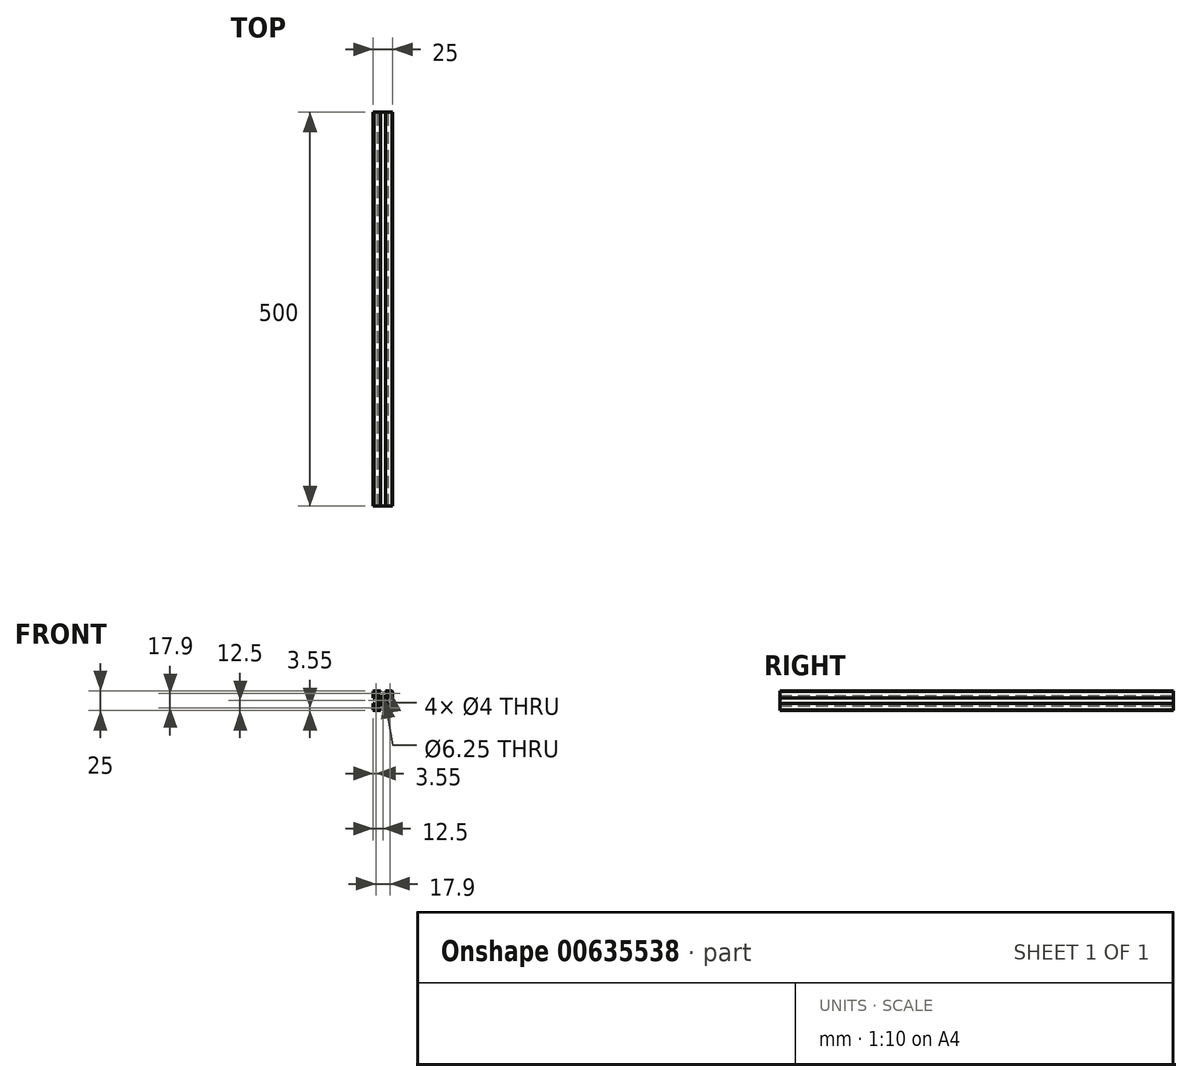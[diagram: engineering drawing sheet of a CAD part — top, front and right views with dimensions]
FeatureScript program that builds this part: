
annotation { "Feature Type Name" : "Feature", "Feature Type Description" : "" }
export const myFeature = defineFeature(function(context is Context, id is Id, definition is map)
    precondition{}
    {
        {
            var Q0;
            Q0=qCreatedBy(makeId("Front.planeOp"),FACE);
            var sketch = newSketch(context, id + "F0", { "sketchPlane" : qUnion([Q0])});
            skLineSegment(sketch, "E0.bottom", {"start": v(0, 0) * mm, "end": v(12.5, 0) * mm, "construction": true});
            skLineSegment(sketch, "E0.top", {"start": v(0, -12.5) * mm, "end": v(12.5, -12.5) * mm, "construction": true});
            skLineSegment(sketch, "E0.left", {"start": v(0, 0) * mm, "end": v(0, -12.5) * mm, "construction": true});
            skLineSegment(sketch, "E0.right", {"start": v(12.5, 0) * mm, "end": v(12.5, -12.5) * mm, "construction": true});
            skLineSegment(sketch, "E1", {"start": v(0, -3.25) * mm, "end": v(12.5, -3.25) * mm, "construction": true});
            skLineSegment(sketch, "E2", {"start": v(0, 0) * mm, "end": v(12.5, -12.5) * mm, "construction": true});
            skLineSegment(sketch, "E3", {"start": v(3.25, 0) * mm, "end": v(3.25, -12.5) * mm, "construction": true});
            skLineSegment(sketch, "E4", {"start": v(12.5, -3.25) * mm, "end": v(12.5, -12.5) * mm});
            skLineSegment(sketch, "E5", {"start": v(3.25, -12.5) * mm, "end": v(12.5, -12.5) * mm});
            skLineSegment(sketch, "E6", {"start": v(0, -5.4) * mm, "end": v(12.5, -5.4) * mm, "construction": true});
            skLineSegment(sketch, "E7", {"start": v(10.8, -3.25) * mm, "end": v(10.8, -12.5) * mm, "construction": true});
            skLineSegment(sketch, "E8", {"start": v(12.5, -3.25) * mm, "end": v(10.8, -3.25) * mm});
            skLineSegment(sketch, "E9", {"start": v(10.8, -3.25) * mm, "end": v(10.8, -5.4) * mm});
            skLineSegment(sketch, "E10", {"start": v(5.4, 0) * mm, "end": v(5.4, -12.5) * mm, "construction": true});
            skLineSegment(sketch, "E11", {"start": v(0, -10.8) * mm, "end": v(12.5, -10.8) * mm, "construction": true});
            skLineSegment(sketch, "E12", {"start": v(3.25, -12.5) * mm, "end": v(3.25, -10.8) * mm});
            skLineSegment(sketch, "E13", {"start": v(3.25, -10.8) * mm, "end": v(5.4, -10.8) * mm});
            skLineSegment(sketch, "E14.MirrorCS", {"start": v(3.25, 10.8) * mm, "end": v(5.4, 10.8) * mm});
            skLineSegment(sketch, "E15.MirrorCS", {"start": v(3.25, 12.5) * mm, "end": v(3.25, 10.8) * mm});
            skLineSegment(sketch, "E16.MirrorCS", {"start": v(10.8, 3.25) * mm, "end": v(10.8, 5.4) * mm});
            skLineSegment(sketch, "E17.MirrorCS", {"start": v(12.5, 3.25) * mm, "end": v(10.8, 3.25) * mm});
            skLineSegment(sketch, "E18.MirrorCS", {"start": v(12.5, 3.25) * mm, "end": v(12.5, 12.5) * mm});
            skLineSegment(sketch, "E19.MirrorCS", {"start": v(3.25, 12.5) * mm, "end": v(12.5, 12.5) * mm});
            skLineSegment(sketch, "E20.MirrorCS", {"start": v(-3.25, 10.8) * mm, "end": v(-5.4, 10.8) * mm});
            skLineSegment(sketch, "E21.MirrorCS", {"start": v(-3.25, 12.5) * mm, "end": v(-3.25, 10.8) * mm});
            skLineSegment(sketch, "E22.MirrorCS", {"start": v(-3.25, 12.5) * mm, "end": v(-12.5, 12.5) * mm});
            skLineSegment(sketch, "E23.MirrorCS", {"start": v(-12.5, 3.25) * mm, "end": v(-12.5, 12.5) * mm});
            skLineSegment(sketch, "E24.MirrorCS", {"start": v(-12.5, 3.25) * mm, "end": v(-10.8, 3.25) * mm});
            skLineSegment(sketch, "E25.MirrorCS", {"start": v(-10.8, 3.25) * mm, "end": v(-10.8, 5.4) * mm});
            skLineSegment(sketch, "E26.MirrorCS", {"start": v(-10.8, -3.25) * mm, "end": v(-10.8, -5.4) * mm});
            skLineSegment(sketch, "E27.MirrorCS", {"start": v(-12.5, -3.25) * mm, "end": v(-10.8, -3.25) * mm});
            skLineSegment(sketch, "E28.MirrorCS", {"start": v(-12.5, -3.25) * mm, "end": v(-12.5, -12.5) * mm});
            skLineSegment(sketch, "E29.MirrorCS", {"start": v(-3.25, -12.5) * mm, "end": v(-12.5, -12.5) * mm});
            skLineSegment(sketch, "E30.MirrorCS", {"start": v(-3.25, -12.5) * mm, "end": v(-3.25, -10.8) * mm});
            skLineSegment(sketch, "E31.MirrorCS", {"start": v(-3.25, -10.8) * mm, "end": v(-5.4, -10.8) * mm});
            skLineSegment(sketch, "E32", {"start": v(6.25, -5.4) * mm, "end": v(6.25, -12.5) * mm, "construction": true});
            skLineSegment(sketch, "E33", {"start": v(0, -6.25) * mm, "end": v(6.25, -6.25) * mm, "construction": true});
            skLineSegment(sketch, "E34", {"start": v(6.25, -5.4) * mm, "end": v(10.8, -5.4) * mm});
            skLineSegment(sketch, "E35", {"start": v(5.4, -10.8) * mm, "end": v(5.4, -6.25) * mm});
            skLineSegment(sketch, "E36.MirrorCS", {"start": v(6.25, 5.4) * mm, "end": v(10.8, 5.4) * mm});
            skLineSegment(sketch, "E37.MirrorCS", {"start": v(5.4, 10.8) * mm, "end": v(5.4, 6.25) * mm});
            skLineSegment(sketch, "E38.MirrorCS", {"start": v(-5.4, 10.8) * mm, "end": v(-5.4, 6.25) * mm});
            skLineSegment(sketch, "E39.MirrorCS", {"start": v(-6.25, 5.4) * mm, "end": v(-10.8, 5.4) * mm});
            skLineSegment(sketch, "E40.MirrorCS", {"start": v(-6.25, -5.4) * mm, "end": v(-10.8, -5.4) * mm});
            skLineSegment(sketch, "E41.MirrorCS", {"start": v(-5.4, -10.8) * mm, "end": v(-5.4, -6.25) * mm});
            skArc(sketch, "E42", {"start": v(5.4, -6.25) * mm, "mid": v(0, -5.4) * mm, "end": v(-5.4, -6.25) * mm});
            skArc(sketch, "E43.MirrorCS", {"start": v(5.4, 6.25) * mm, "mid": v(0, 5.4) * mm, "end": v(-5.4, 6.25) * mm});
            skArc(sketch, "E44", {"start": v(6.25, 5.4) * mm, "mid": v(5.4, 0) * mm, "end": v(6.25, -5.4) * mm});
            skArc(sketch, "E45.MirrorCS", {"start": v(-6.25, 5.4) * mm, "mid": v(-5.4, 0) * mm, "end": v(-6.25, -5.4) * mm});
            skLineSegment(sketch, "E46", {"start": v(12.5, -5.4) * mm, "end": v(8.95, -8.95) * mm, "construction": true});
            skCircle(sketch, "E47", {"center": v(8.95, -8.95) * mm, "radius": 2 * mm, "construction": true});
            skCircle(sketch, "E48.MirrorC", {"center": v(8.95, 8.95) * mm, "radius": 2 * mm, "construction": true});
            skCircle(sketch, "E49.MirrorC", {"center": v(-8.95, 8.95) * mm, "radius": 2 * mm, "construction": true});
            skCircle(sketch, "E50.MirrorC", {"center": v(-8.95, -8.95) * mm, "radius": 2 * mm, "construction": true});
            skCircle(sketch, "E51", {"center": v(0, 0) * mm, "radius": 3.12 * mm, "construction": true});
            skSolve(sketch);
        }
        {
            var Q0;
            Q0=makeQuery(id+"F0.imprint","IMPRINT",FACE,{"disambiguationData":[TD([[makeQuery(id+"F0.imprint","IMPRINT",EDGE,{"derivedFrom":sQuery(id+"F0.wireOp",EDGE,"E4")}),-1.0]])]});
            extrude(context, id + "F1", {"entities" : qUnion([Q0]), "depth" : 500 * mm, "offsetDistance" : 25 * mm});
        }
        {
            var Q0;
            Q0=makeQuery(id+"F1.opExtrude","SWEPT_EDGE",EDGE,{"disambiguationData":[OSD([sQuery(id+"F0.wireOp",EDGE,"E22.MirrorCS"),sQuery(id+"F0.wireOp",EDGE,"E23.MirrorCS")])]});
            chamfer(context, id + "F2", {"entities" : qUnion([Q0]), "width" : 1 * mm, "tangentPropagation" : true});
        }
        {
            var Q0;
            Q0=makeQuery(id+"F1.opExtrude","SWEPT_EDGE",EDGE,{"disambiguationData":[OSD([sQuery(id+"F0.wireOp",EDGE,"E18.MirrorCS"),sQuery(id+"F0.wireOp",EDGE,"E19.MirrorCS")])]});
            var Q1;
            Q1=makeQuery(id+"F1.opExtrude","SWEPT_EDGE",EDGE,{"disambiguationData":[OSD([sQuery(id+"F0.wireOp",EDGE,"E4"),sQuery(id+"F0.wireOp",EDGE,"E5")])]});
            var Q2;
            Q2=makeQuery(id+"F1.opExtrude","SWEPT_EDGE",EDGE,{"disambiguationData":[OSD([sQuery(id+"F0.wireOp",EDGE,"E28.MirrorCS"),sQuery(id+"F0.wireOp",EDGE,"E29.MirrorCS")])]});
            chamfer(context, id + "F3", {"entities" : qUnion([Q0, Q1, Q2]), "width" : 1 * mm, "tangentPropagation" : true});
        }
        {
            var Q0;
            Q0=makeQuery(id+"F1.opExtrude","SWEPT_EDGE",EDGE,{"disambiguationData":[OSD([sQuery(id+"F0.wireOp",EDGE,"E14.MirrorCS"),sQuery(id+"F0.wireOp",EDGE,"E15.MirrorCS")])]});
            var Q1;
            Q1=makeQuery(id+"F1.opExtrude","SWEPT_EDGE",EDGE,{"disambiguationData":[OSD([sQuery(id+"F0.wireOp",EDGE,"E16.MirrorCS"),sQuery(id+"F0.wireOp",EDGE,"E17.MirrorCS")])]});
            var Q2;
            Q2=makeQuery(id+"F1.opExtrude","SWEPT_EDGE",EDGE,{"disambiguationData":[OSD([sQuery(id+"F0.wireOp",EDGE,"E8"),sQuery(id+"F0.wireOp",EDGE,"E9")])]});
            var Q3;
            Q3=makeQuery(id+"F1.opExtrude","SWEPT_EDGE",EDGE,{"disambiguationData":[OSD([sQuery(id+"F0.wireOp",EDGE,"E12"),sQuery(id+"F0.wireOp",EDGE,"E13")])]});
            var Q4;
            Q4=makeQuery(id+"F1.opExtrude","SWEPT_EDGE",EDGE,{"disambiguationData":[OSD([sQuery(id+"F0.wireOp",EDGE,"E30.MirrorCS"),sQuery(id+"F0.wireOp",EDGE,"E31.MirrorCS")])]});
            var Q5;
            Q5=makeQuery(id+"F1.opExtrude","SWEPT_EDGE",EDGE,{"disambiguationData":[OSD([sQuery(id+"F0.wireOp",EDGE,"E26.MirrorCS"),sQuery(id+"F0.wireOp",EDGE,"E27.MirrorCS")])]});
            var Q6;
            Q6=makeQuery(id+"F1.opExtrude","SWEPT_EDGE",EDGE,{"disambiguationData":[OSD([sQuery(id+"F0.wireOp",EDGE,"E20.MirrorCS"),sQuery(id+"F0.wireOp",EDGE,"E21.MirrorCS")])]});
            var Q7;
            Q7=makeQuery(id+"F1.opExtrude","SWEPT_EDGE",EDGE,{"disambiguationData":[OSD([sQuery(id+"F0.wireOp",EDGE,"E24.MirrorCS"),sQuery(id+"F0.wireOp",EDGE,"E25.MirrorCS")])]});
            chamfer(context, id + "F4", {"entities" : qUnion([Q0, Q1, Q2, Q3, Q4, Q5, Q6, Q7]), "width" : 1 * mm, "tangentPropagation" : true});
        }
        {
            var Q0;
            Q0=sQuery(id+"F0.wireOp",VERTEX,"E47.center");
            var Q1;
            Q1=makeQuery(id+"F1.opExtrude","SWEPT_BODY",BODY,{"disambiguationData":[OSD([sQuery(id+"F0.wireOp",EDGE,"E4"),sQuery(id+"F0.wireOp",EDGE,"E5"),sQuery(id+"F0.wireOp",EDGE,"E8"),sQuery(id+"F0.wireOp",EDGE,"E9"),sQuery(id+"F0.wireOp",EDGE,"E12"),sQuery(id+"F0.wireOp",EDGE,"E13"),sQuery(id+"F0.wireOp",EDGE,"E14.MirrorCS"),sQuery(id+"F0.wireOp",EDGE,"E15.MirrorCS"),sQuery(id+"F0.wireOp",EDGE,"E16.MirrorCS"),sQuery(id+"F0.wireOp",EDGE,"E17.MirrorCS"),sQuery(id+"F0.wireOp",EDGE,"E18.MirrorCS"),sQuery(id+"F0.wireOp",EDGE,"E19.MirrorCS"),sQuery(id+"F0.wireOp",EDGE,"E20.MirrorCS"),sQuery(id+"F0.wireOp",EDGE,"E21.MirrorCS"),sQuery(id+"F0.wireOp",EDGE,"E22.MirrorCS"),sQuery(id+"F0.wireOp",EDGE,"E23.MirrorCS"),sQuery(id+"F0.wireOp",EDGE,"E24.MirrorCS"),sQuery(id+"F0.wireOp",EDGE,"E25.MirrorCS"),sQuery(id+"F0.wireOp",EDGE,"E26.MirrorCS"),sQuery(id+"F0.wireOp",EDGE,"E27.MirrorCS"),sQuery(id+"F0.wireOp",EDGE,"E28.MirrorCS"),sQuery(id+"F0.wireOp",EDGE,"E29.MirrorCS"),sQuery(id+"F0.wireOp",EDGE,"E30.MirrorCS"),sQuery(id+"F0.wireOp",EDGE,"E31.MirrorCS"),sQuery(id+"F0.wireOp",EDGE,"E34"),sQuery(id+"F0.wireOp",EDGE,"E35"),sQuery(id+"F0.wireOp",EDGE,"E36.MirrorCS"),sQuery(id+"F0.wireOp",EDGE,"E37.MirrorCS"),sQuery(id+"F0.wireOp",EDGE,"E38.MirrorCS"),sQuery(id+"F0.wireOp",EDGE,"E39.MirrorCS"),sQuery(id+"F0.wireOp",EDGE,"E40.MirrorCS"),sQuery(id+"F0.wireOp",EDGE,"E41.MirrorCS"),sQuery(id+"F0.wireOp",EDGE,"E42"),sQuery(id+"F0.wireOp",EDGE,"E43.MirrorCS"),sQuery(id+"F0.wireOp",EDGE,"E44"),sQuery(id+"F0.wireOp",EDGE,"E45.MirrorCS")])]});
            hole(context, id + "F5", {"style" : HoleStyle.SIMPLE, "endStyle" : HoleEndStyle.THROUGH, "oppositeDirection" : true, "holeDiameter" : 4 * mm, "majorDiameter" : 5 * mm, "isTappedThrough" : true, "tappedDepth" : 12 * mm, "tapClearance" : 3, "locations" : qUnion([Q0]), "scope" : qUnion([Q1])});
        }
        {
            var Q0;
            Q0=sQuery(id+"F0.wireOp",VERTEX,"E48.MirrorC.center");
            var Q1;
            Q1=makeQuery(id+"F1.opExtrude","SWEPT_BODY",BODY,{"disambiguationData":[OSD([sQuery(id+"F0.wireOp",EDGE,"E4"),sQuery(id+"F0.wireOp",EDGE,"E5"),sQuery(id+"F0.wireOp",EDGE,"E8"),sQuery(id+"F0.wireOp",EDGE,"E9"),sQuery(id+"F0.wireOp",EDGE,"E12"),sQuery(id+"F0.wireOp",EDGE,"E13"),sQuery(id+"F0.wireOp",EDGE,"E14.MirrorCS"),sQuery(id+"F0.wireOp",EDGE,"E15.MirrorCS"),sQuery(id+"F0.wireOp",EDGE,"E16.MirrorCS"),sQuery(id+"F0.wireOp",EDGE,"E17.MirrorCS"),sQuery(id+"F0.wireOp",EDGE,"E18.MirrorCS"),sQuery(id+"F0.wireOp",EDGE,"E19.MirrorCS"),sQuery(id+"F0.wireOp",EDGE,"E20.MirrorCS"),sQuery(id+"F0.wireOp",EDGE,"E21.MirrorCS"),sQuery(id+"F0.wireOp",EDGE,"E22.MirrorCS"),sQuery(id+"F0.wireOp",EDGE,"E23.MirrorCS"),sQuery(id+"F0.wireOp",EDGE,"E24.MirrorCS"),sQuery(id+"F0.wireOp",EDGE,"E25.MirrorCS"),sQuery(id+"F0.wireOp",EDGE,"E26.MirrorCS"),sQuery(id+"F0.wireOp",EDGE,"E27.MirrorCS"),sQuery(id+"F0.wireOp",EDGE,"E28.MirrorCS"),sQuery(id+"F0.wireOp",EDGE,"E29.MirrorCS"),sQuery(id+"F0.wireOp",EDGE,"E30.MirrorCS"),sQuery(id+"F0.wireOp",EDGE,"E31.MirrorCS"),sQuery(id+"F0.wireOp",EDGE,"E34"),sQuery(id+"F0.wireOp",EDGE,"E35"),sQuery(id+"F0.wireOp",EDGE,"E36.MirrorCS"),sQuery(id+"F0.wireOp",EDGE,"E37.MirrorCS"),sQuery(id+"F0.wireOp",EDGE,"E38.MirrorCS"),sQuery(id+"F0.wireOp",EDGE,"E39.MirrorCS"),sQuery(id+"F0.wireOp",EDGE,"E40.MirrorCS"),sQuery(id+"F0.wireOp",EDGE,"E41.MirrorCS"),sQuery(id+"F0.wireOp",EDGE,"E42"),sQuery(id+"F0.wireOp",EDGE,"E43.MirrorCS"),sQuery(id+"F0.wireOp",EDGE,"E44"),sQuery(id+"F0.wireOp",EDGE,"E45.MirrorCS")])]});
            hole(context, id + "F6", {"style" : HoleStyle.SIMPLE, "endStyle" : HoleEndStyle.THROUGH, "oppositeDirection" : true, "holeDiameter" : 4 * mm, "majorDiameter" : 5 * mm, "isTappedThrough" : true, "tappedDepth" : 12 * mm, "tapClearance" : 3, "locations" : qUnion([Q0]), "scope" : qUnion([Q1])});
        }
        {
            var Q0;
            Q0=sQuery(id+"F0.wireOp",VERTEX,"E50.MirrorC.center");
            var Q1;
            Q1=makeQuery(id+"F1.opExtrude","SWEPT_BODY",BODY,{"disambiguationData":[OSD([sQuery(id+"F0.wireOp",EDGE,"E4"),sQuery(id+"F0.wireOp",EDGE,"E5"),sQuery(id+"F0.wireOp",EDGE,"E8"),sQuery(id+"F0.wireOp",EDGE,"E9"),sQuery(id+"F0.wireOp",EDGE,"E12"),sQuery(id+"F0.wireOp",EDGE,"E13"),sQuery(id+"F0.wireOp",EDGE,"E14.MirrorCS"),sQuery(id+"F0.wireOp",EDGE,"E15.MirrorCS"),sQuery(id+"F0.wireOp",EDGE,"E16.MirrorCS"),sQuery(id+"F0.wireOp",EDGE,"E17.MirrorCS"),sQuery(id+"F0.wireOp",EDGE,"E18.MirrorCS"),sQuery(id+"F0.wireOp",EDGE,"E19.MirrorCS"),sQuery(id+"F0.wireOp",EDGE,"E20.MirrorCS"),sQuery(id+"F0.wireOp",EDGE,"E21.MirrorCS"),sQuery(id+"F0.wireOp",EDGE,"E22.MirrorCS"),sQuery(id+"F0.wireOp",EDGE,"E23.MirrorCS"),sQuery(id+"F0.wireOp",EDGE,"E24.MirrorCS"),sQuery(id+"F0.wireOp",EDGE,"E25.MirrorCS"),sQuery(id+"F0.wireOp",EDGE,"E26.MirrorCS"),sQuery(id+"F0.wireOp",EDGE,"E27.MirrorCS"),sQuery(id+"F0.wireOp",EDGE,"E28.MirrorCS"),sQuery(id+"F0.wireOp",EDGE,"E29.MirrorCS"),sQuery(id+"F0.wireOp",EDGE,"E30.MirrorCS"),sQuery(id+"F0.wireOp",EDGE,"E31.MirrorCS"),sQuery(id+"F0.wireOp",EDGE,"E34"),sQuery(id+"F0.wireOp",EDGE,"E35"),sQuery(id+"F0.wireOp",EDGE,"E36.MirrorCS"),sQuery(id+"F0.wireOp",EDGE,"E37.MirrorCS"),sQuery(id+"F0.wireOp",EDGE,"E38.MirrorCS"),sQuery(id+"F0.wireOp",EDGE,"E39.MirrorCS"),sQuery(id+"F0.wireOp",EDGE,"E40.MirrorCS"),sQuery(id+"F0.wireOp",EDGE,"E41.MirrorCS"),sQuery(id+"F0.wireOp",EDGE,"E42"),sQuery(id+"F0.wireOp",EDGE,"E43.MirrorCS"),sQuery(id+"F0.wireOp",EDGE,"E44"),sQuery(id+"F0.wireOp",EDGE,"E45.MirrorCS")])]});
            hole(context, id + "F7", {"style" : HoleStyle.SIMPLE, "endStyle" : HoleEndStyle.THROUGH, "oppositeDirection" : true, "holeDiameter" : 4 * mm, "majorDiameter" : 5 * mm, "isTappedThrough" : true, "tappedDepth" : 12 * mm, "tapClearance" : 3, "locations" : qUnion([Q0]), "scope" : qUnion([Q1])});
        }
        {
            var Q0;
            Q0=sQuery(id+"F0.wireOp",VERTEX,"E49.MirrorC.center");
            var Q1;
            Q1=makeQuery(id+"F1.opExtrude","SWEPT_BODY",BODY,{"disambiguationData":[OSD([sQuery(id+"F0.wireOp",EDGE,"E4"),sQuery(id+"F0.wireOp",EDGE,"E5"),sQuery(id+"F0.wireOp",EDGE,"E8"),sQuery(id+"F0.wireOp",EDGE,"E9"),sQuery(id+"F0.wireOp",EDGE,"E12"),sQuery(id+"F0.wireOp",EDGE,"E13"),sQuery(id+"F0.wireOp",EDGE,"E14.MirrorCS"),sQuery(id+"F0.wireOp",EDGE,"E15.MirrorCS"),sQuery(id+"F0.wireOp",EDGE,"E16.MirrorCS"),sQuery(id+"F0.wireOp",EDGE,"E17.MirrorCS"),sQuery(id+"F0.wireOp",EDGE,"E18.MirrorCS"),sQuery(id+"F0.wireOp",EDGE,"E19.MirrorCS"),sQuery(id+"F0.wireOp",EDGE,"E20.MirrorCS"),sQuery(id+"F0.wireOp",EDGE,"E21.MirrorCS"),sQuery(id+"F0.wireOp",EDGE,"E22.MirrorCS"),sQuery(id+"F0.wireOp",EDGE,"E23.MirrorCS"),sQuery(id+"F0.wireOp",EDGE,"E24.MirrorCS"),sQuery(id+"F0.wireOp",EDGE,"E25.MirrorCS"),sQuery(id+"F0.wireOp",EDGE,"E26.MirrorCS"),sQuery(id+"F0.wireOp",EDGE,"E27.MirrorCS"),sQuery(id+"F0.wireOp",EDGE,"E28.MirrorCS"),sQuery(id+"F0.wireOp",EDGE,"E29.MirrorCS"),sQuery(id+"F0.wireOp",EDGE,"E30.MirrorCS"),sQuery(id+"F0.wireOp",EDGE,"E31.MirrorCS"),sQuery(id+"F0.wireOp",EDGE,"E34"),sQuery(id+"F0.wireOp",EDGE,"E35"),sQuery(id+"F0.wireOp",EDGE,"E36.MirrorCS"),sQuery(id+"F0.wireOp",EDGE,"E37.MirrorCS"),sQuery(id+"F0.wireOp",EDGE,"E38.MirrorCS"),sQuery(id+"F0.wireOp",EDGE,"E39.MirrorCS"),sQuery(id+"F0.wireOp",EDGE,"E40.MirrorCS"),sQuery(id+"F0.wireOp",EDGE,"E41.MirrorCS"),sQuery(id+"F0.wireOp",EDGE,"E42"),sQuery(id+"F0.wireOp",EDGE,"E43.MirrorCS"),sQuery(id+"F0.wireOp",EDGE,"E44"),sQuery(id+"F0.wireOp",EDGE,"E45.MirrorCS")])]});
            hole(context, id + "F8", {"style" : HoleStyle.SIMPLE, "endStyle" : HoleEndStyle.THROUGH, "oppositeDirection" : true, "holeDiameter" : 4 * mm, "majorDiameter" : 5 * mm, "isTappedThrough" : true, "tappedDepth" : 12 * mm, "tapClearance" : 3, "locations" : qUnion([Q0]), "scope" : qUnion([Q1])});
        }
        {
            var Q0;
            Q0=sQuery(id+"F0.wireOp",VERTEX,"E2.start");
            var Q1;
            Q1=makeQuery(id+"F1.opExtrude","SWEPT_BODY",BODY,{"disambiguationData":[OSD([sQuery(id+"F0.wireOp",EDGE,"E4"),sQuery(id+"F0.wireOp",EDGE,"E5"),sQuery(id+"F0.wireOp",EDGE,"E8"),sQuery(id+"F0.wireOp",EDGE,"E9"),sQuery(id+"F0.wireOp",EDGE,"E12"),sQuery(id+"F0.wireOp",EDGE,"E13"),sQuery(id+"F0.wireOp",EDGE,"E14.MirrorCS"),sQuery(id+"F0.wireOp",EDGE,"E15.MirrorCS"),sQuery(id+"F0.wireOp",EDGE,"E16.MirrorCS"),sQuery(id+"F0.wireOp",EDGE,"E17.MirrorCS"),sQuery(id+"F0.wireOp",EDGE,"E18.MirrorCS"),sQuery(id+"F0.wireOp",EDGE,"E19.MirrorCS"),sQuery(id+"F0.wireOp",EDGE,"E20.MirrorCS"),sQuery(id+"F0.wireOp",EDGE,"E21.MirrorCS"),sQuery(id+"F0.wireOp",EDGE,"E22.MirrorCS"),sQuery(id+"F0.wireOp",EDGE,"E23.MirrorCS"),sQuery(id+"F0.wireOp",EDGE,"E24.MirrorCS"),sQuery(id+"F0.wireOp",EDGE,"E25.MirrorCS"),sQuery(id+"F0.wireOp",EDGE,"E26.MirrorCS"),sQuery(id+"F0.wireOp",EDGE,"E27.MirrorCS"),sQuery(id+"F0.wireOp",EDGE,"E28.MirrorCS"),sQuery(id+"F0.wireOp",EDGE,"E29.MirrorCS"),sQuery(id+"F0.wireOp",EDGE,"E30.MirrorCS"),sQuery(id+"F0.wireOp",EDGE,"E31.MirrorCS"),sQuery(id+"F0.wireOp",EDGE,"E34"),sQuery(id+"F0.wireOp",EDGE,"E35"),sQuery(id+"F0.wireOp",EDGE,"E36.MirrorCS"),sQuery(id+"F0.wireOp",EDGE,"E37.MirrorCS"),sQuery(id+"F0.wireOp",EDGE,"E38.MirrorCS"),sQuery(id+"F0.wireOp",EDGE,"E39.MirrorCS"),sQuery(id+"F0.wireOp",EDGE,"E40.MirrorCS"),sQuery(id+"F0.wireOp",EDGE,"E41.MirrorCS"),sQuery(id+"F0.wireOp",EDGE,"E42"),sQuery(id+"F0.wireOp",EDGE,"E43.MirrorCS"),sQuery(id+"F0.wireOp",EDGE,"E44"),sQuery(id+"F0.wireOp",EDGE,"E45.MirrorCS")])]});
            hole(context, id + "F9", {"style" : HoleStyle.SIMPLE, "endStyle" : HoleEndStyle.THROUGH, "oppositeDirection" : true, "holeDiameter" : 6.25 * mm, "majorDiameter" : 5 * mm, "isTappedThrough" : true, "tappedDepth" : 12 * mm, "tapClearance" : 3, "locations" : qUnion([Q0]), "scope" : qUnion([Q1])});
        }
    });
